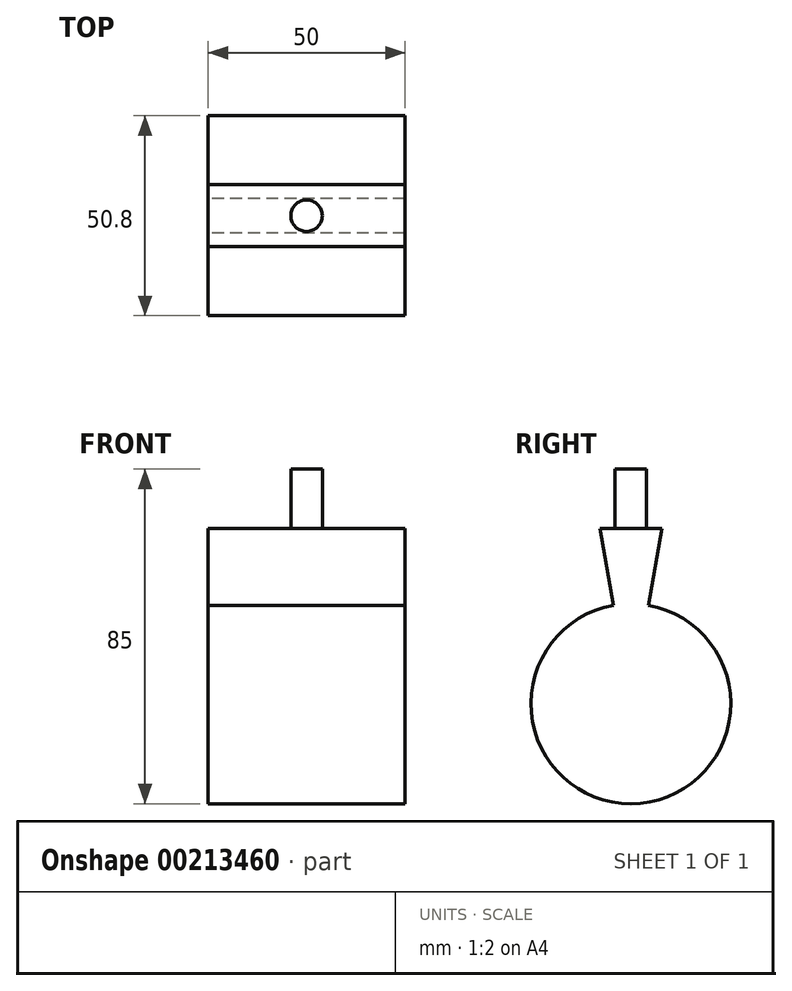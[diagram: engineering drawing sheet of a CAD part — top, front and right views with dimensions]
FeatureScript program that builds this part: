
annotation { "Feature Type Name" : "Feature", "Feature Type Description" : "" }
export const myFeature = defineFeature(function(context is Context, id is Id, definition is map)
    precondition{}
    {
        {
            var Q0;
            Q0=qCreatedBy(makeId("Right.planeOp"),FACE);
            var sketch = newSketch(context, id + "F0", { "sketchPlane" : qUnion([Q0])});
            skArc(sketch, "E0", {"start": v(-4.41, -19.59) * mm, "mid": v(0, -70) * mm, "end": v(4.41, -19.59) * mm});
            skLineSegment(sketch, "E1", {"start": v(-4.41, -19.59) * mm, "end": v(-7.86, 0) * mm});
            skLineSegment(sketch, "E2", {"start": v(0, -44.6) * mm, "end": v(0, -31.4) * mm, "construction": true});
            skLineSegment(sketch, "E3.MirrorCS", {"start": v(4.41, -19.59) * mm, "end": v(7.86, 0) * mm});
            skLineSegment(sketch, "E4", {"start": v(-7.86, 0) * mm, "end": v(7.86, 0) * mm});
            skLineSegment(sketch, "E5", {"start": v(0, -44.6) * mm, "end": v(0, -108.78) * mm, "construction": true});
            skPoint(sketch, "E5.endSnap0", {"position": v(0, -70) * mm});
            skSolve(sketch);
        }
        {
            var Q0;
            Q0=makeQuery(id+"F0.imprint","IMPRINT",FACE,{"disambiguationData":[TD([[makeQuery(id+"F0.imprint","IMPRINT",EDGE,{"derivedFrom":sQuery(id+"F0.wireOp",EDGE,"E0")}),1.0]])]});
            extrude(context, id + "F1", {"entities" : qUnion([Q0]), "depth" : 50 * mm});
        }
        {
            var Q0;
            Q0=makeQuery(id+"F1.opExtrude","SWEPT_FACE",FACE,{"disambiguationData":[OSD([sQuery(id+"F0.wireOp",EDGE,"E4")])]});
            var sketch = newSketch(context, id + "F2", { "sketchPlane" : qUnion([Q0])});
            skLineSegment(sketch, "E6", {"start": v(0, 0) * mm, "end": v(50, 0) * mm, "construction": true});
            skLineSegment(sketch, "E7", {"start": v(25, 7.86) * mm, "end": v(25, -7.86) * mm, "construction": true});
            skCircle(sketch, "E8", {"center": v(25, 0) * mm, "radius": 4 * mm});
            skSolve(sketch);
        }
        {
            var Q0;
            Q0=makeQuery(id+"F2.imprint","IMPRINT",FACE,{"disambiguationData":[TD([[makeQuery(id+"F2.imprint","IMPRINT",EDGE,{"derivedFrom":sQuery(id+"F2.wireOp",EDGE,"E8")}),1.0]])]});
            extrude(context, id + "F3", {"entities" : qUnion([Q0]), "operationType" : NewBodyOperationType.ADD, "depth" : 15 * mm});
        }
    });
